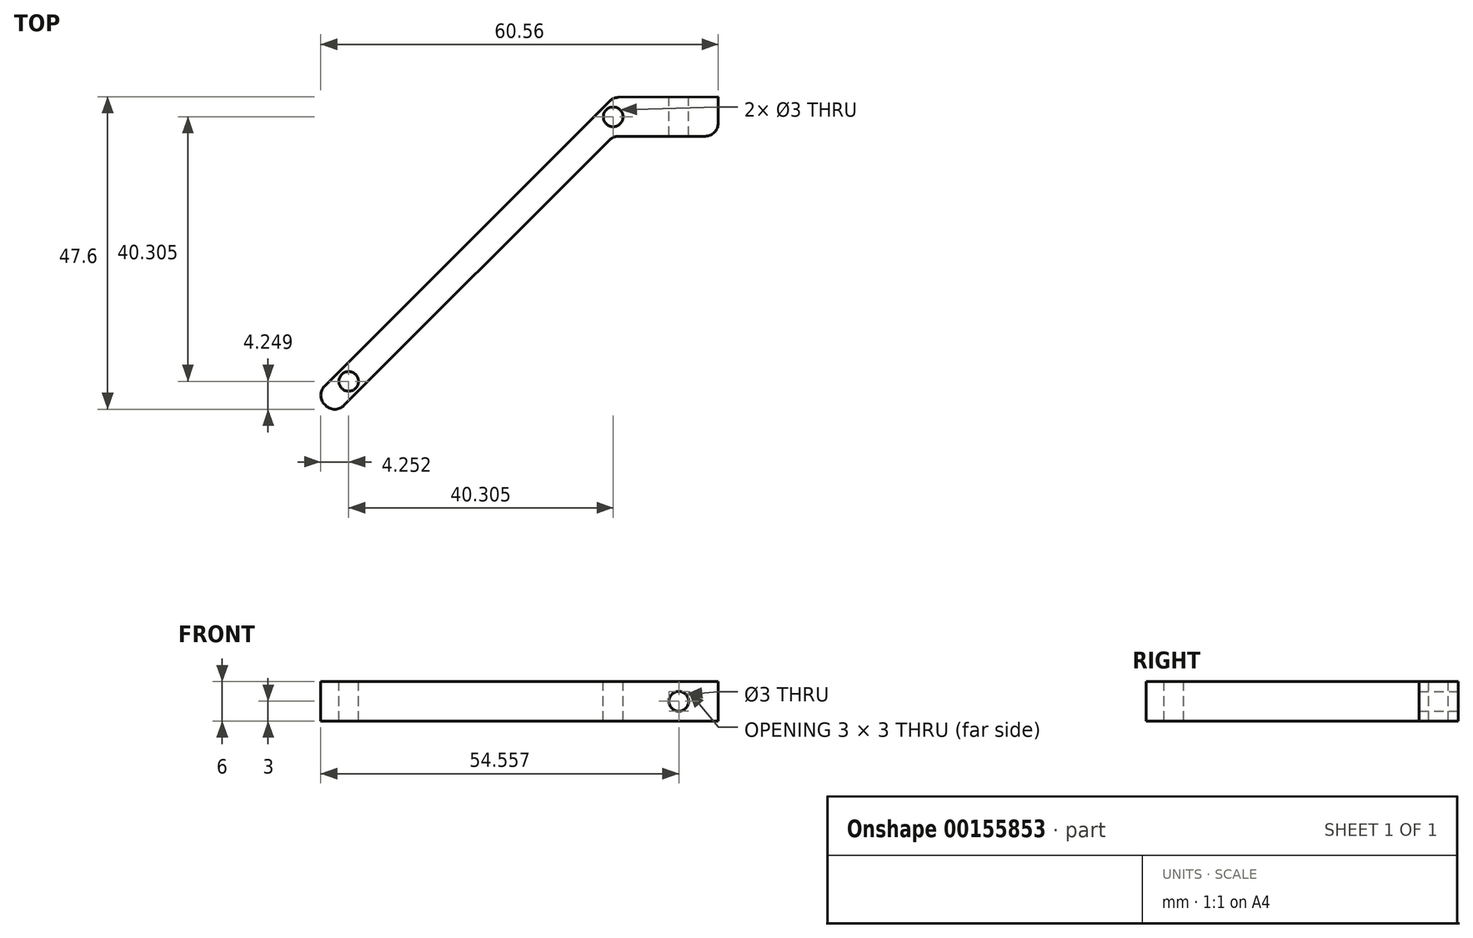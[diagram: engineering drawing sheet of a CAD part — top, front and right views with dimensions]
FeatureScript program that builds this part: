
annotation { "Feature Type Name" : "Feature", "Feature Type Description" : "" }
export const myFeature = defineFeature(function(context is Context, id is Id, definition is map)
    precondition{}
    {
        {
            var Q0;
            Q0=qCreatedBy(makeId("Top.planeOp"),FACE);
            var sketch = newSketch(context, id + "F0", { "sketchPlane" : qUnion([Q0])});
            skLineSegment(sketch, "E0", {"start": v(-20.56, 4.7) * mm, "end": v(-20.56, -1.3) * mm});
            skLineSegment(sketch, "E1", {"start": v(-20.56, -1.3) * mm, "end": v(-36.56, -1.3) * mm});
            skLineSegment(sketch, "E2", {"start": v(-36.56, -1.3) * mm, "end": v(-36.56, 0.16) * mm});
            skLineSegment(sketch, "E3", {"start": v(-36.56, 4.62) * mm, "end": v(-20.56, 4.7) * mm});
            skLineSegment(sketch, "E4", {"start": v(-36.56, 4.62) * mm, "end": v(-81.94, -40.76) * mm});
            skLineSegment(sketch, "E5", {"start": v(-36.56, -1.3) * mm, "end": v(-78.99, -43.72) * mm});
            skLineSegment(sketch, "E6", {"start": v(-81.94, -40.76) * mm, "end": v(-78.99, -43.72) * mm});
            skLineSegment(sketch, "E7", {"start": v(-36.56, 1.66) * mm, "end": v(-76.87, -38.64) * mm, "construction": true});
            skCircle(sketch, "E8", {"center": v(-76.87, -38.64) * mm, "radius": 1.5 * mm});
            skArc(sketch, "E9", {"start": v(-36.56, 3.16) * mm, "mid": v(-38.06, 1.66) * mm, "end": v(-36.56, 0.16) * mm});
            skArc(sketch, "E10", {"start": v(-36.56, 0.16) * mm, "mid": v(-35.06, 1.66) * mm, "end": v(-36.56, 3.16) * mm});
            skLineSegment(sketch, "E11.trimOffspring", {"start": v(-36.56, 3.16) * mm, "end": v(-36.56, 4.62) * mm});
            skSolve(sketch);
        }
        {
            var Q0;
            Q0=makeQuery(id+"F0.imprint","IMPRINT",FACE,{"disambiguationData":[TD([[makeQuery(id+"F0.imprint","IMPRINT",EDGE,{"derivedFrom":sQuery(id+"F0.wireOp",EDGE,"E0")}),-1.0]])]});
            extrude(context, id + "F1", {"entities" : qUnion([Q0]), "oppositeDirection" : true, "depth" : 6 * mm});
        }
        {
            var Q0;
            Q0=makeQuery(id+"F0.imprint","IMPRINT",FACE,{"disambiguationData":[TD([[makeQuery(id+"F0.imprint","IMPRINT",EDGE,{"derivedFrom":sQuery(id+"F0.wireOp",EDGE,"E2")}),1.0]])]});
            var Q1;
            Q1 = qConstructionFilter(qBodyType(qCreatedBy(id + "F0" ,EDGE), BodyType.WIRE), ConstructionObject.NO);
            extrude(context, id + "F2", {"entities" : qUnion([Q0]), "operationType" : NewBodyOperationType.ADD, "surfaceEntities" : qUnion([Q1]), "oppositeDirection" : true, "depth" : 6 * mm});
        }
        {
            var Q0;
            Q0=qCreatedBy(makeId("Front.planeOp"),FACE);
            var sketch = newSketch(context, id + "F3", { "sketchPlane" : qUnion([Q0])});
            skLineSegment(sketch, "E12", {"start": v(-20.56, -3) * mm, "end": v(-26.56, -3) * mm, "construction": true});
            skCircle(sketch, "E13", {"center": v(-26.56, -3) * mm, "radius": 1.5 * mm});
            skSolve(sketch);
        }
        {
            var Q0;
            Q0 = qSketchRegion(id + "F3", true);
            extrude(context, id + "F4", {"entities" : qUnion([Q0]), "operationType" : NewBodyOperationType.REMOVE, "endBound" : BoundingType.SYMMETRIC, "depth" : 25 * mm});
        }
        {
            var Q0;
            {var subQ0=sQuery(id+"F0.wireOp",EDGE,"E11.trimOffspring");var subQ1=sQuery(id+"F0.wireOp",EDGE,"E4");var subQ2=sQuery(id+"F0.wireOp",EDGE,"E3");Q0=makeQuery(id+"F2.boolean.opBoolean","MERGE",EDGE,{"derivedFrom":[makeQuery(id+"F1.opExtrude","SWEPT_EDGE",EDGE,{"disambiguationData":[OSD([subQ2,subQ1,subQ0])]}),makeQuery(id+"F2.opExtrude","SWEPT_EDGE",EDGE,{"disambiguationData":[OSD([subQ2,subQ1,subQ0])]})]});}
            var Q1;
            Q1=makeQuery(id+"F1.opExtrude","SWEPT_EDGE",EDGE,{"disambiguationData":[OSD([sQuery(id+"F0.wireOp",EDGE,"E0"),sQuery(id+"F0.wireOp",EDGE,"E1")])]});
            var Q2;
            {var subQ0=sQuery(id+"F0.wireOp",EDGE,"E5");var subQ1=sQuery(id+"F0.wireOp",EDGE,"E2");var subQ2=sQuery(id+"F0.wireOp",EDGE,"E1");Q2=makeQuery(id+"F2.boolean.opBoolean","MERGE",EDGE,{"derivedFrom":[makeQuery(id+"F1.opExtrude","SWEPT_EDGE",EDGE,{"disambiguationData":[OSD([subQ2,subQ1,subQ0])]}),makeQuery(id+"F2.opExtrude","SWEPT_EDGE",EDGE,{"disambiguationData":[OSD([subQ2,subQ1,subQ0])]})]});}
            var Q3;
            Q3=makeQuery(id+"F2.opExtrude","SWEPT_EDGE",EDGE,{"disambiguationData":[OSD([sQuery(id+"F0.wireOp",EDGE,"E5"),sQuery(id+"F0.wireOp",EDGE,"E6")])]});
            var Q4;
            Q4=makeQuery(id+"F2.opExtrude","SWEPT_EDGE",EDGE,{"disambiguationData":[OSD([sQuery(id+"F0.wireOp",EDGE,"E4"),sQuery(id+"F0.wireOp",EDGE,"E6")])]});
            fillet(context, id + "F5", {"entities" : qUnion([Q0, Q1, Q2, Q3, Q4]), "radius" : 2 * mm, "tangentPropagation" : true, "allowEdgeOverflow" : false});
        }
    });
